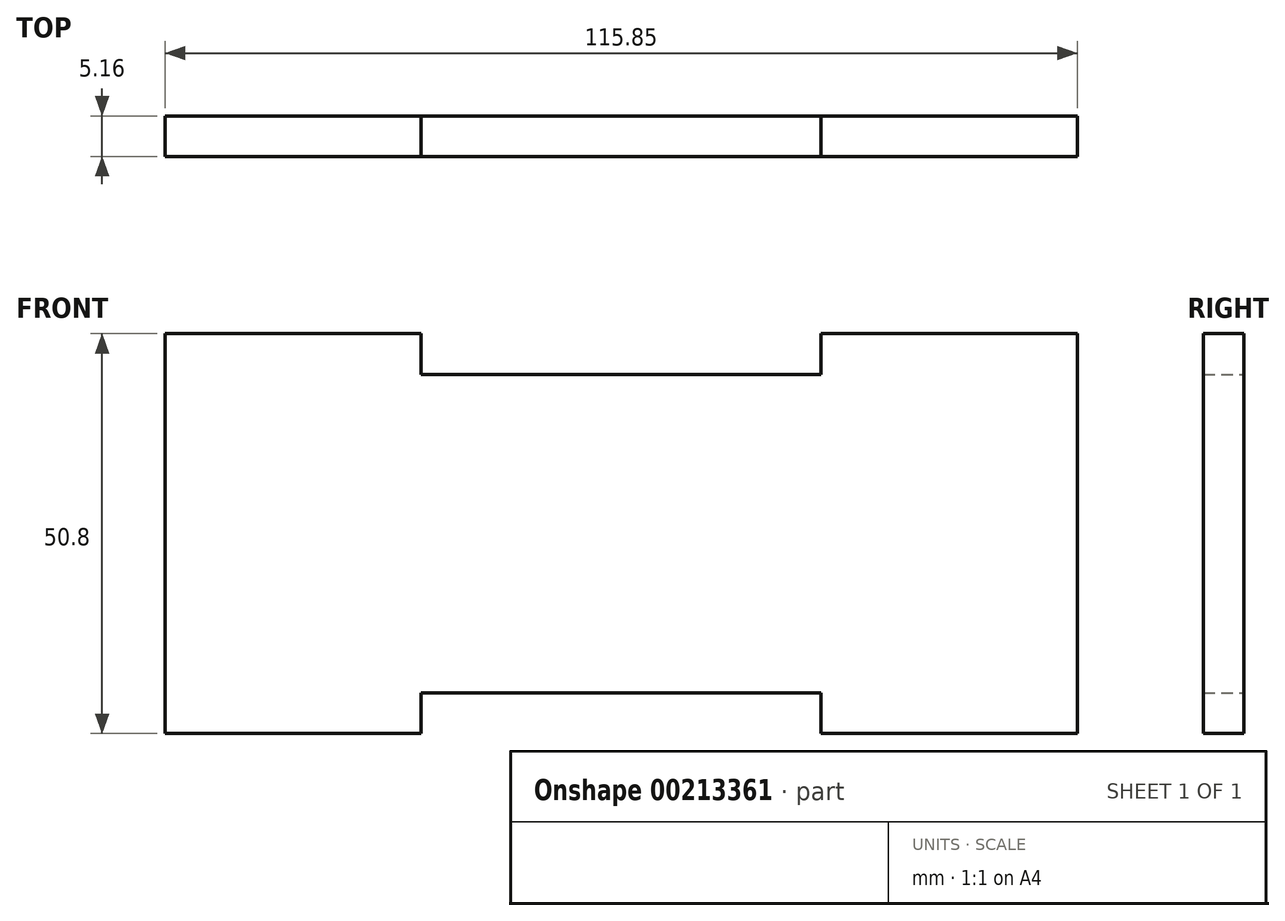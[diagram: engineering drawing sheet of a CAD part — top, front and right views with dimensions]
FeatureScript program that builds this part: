
annotation { "Feature Type Name" : "Feature", "Feature Type Description" : "" }
export const myFeature = defineFeature(function(context is Context, id is Id, definition is map)
    precondition{}
    {
        {
            var Q0;
            Q0=qCreatedBy(makeId("Front.planeOp"),FACE);
            var sketch = newSketch(context, id + "F0", { "sketchPlane" : qUnion([Q0])});
            skLineSegment(sketch, "E0.bottom", {"start": v(0, 0) * mm, "end": v(115.85, 0) * mm});
            skLineSegment(sketch, "E0.top", {"start": v(0, 50.8) * mm, "end": v(115.85, 50.8) * mm});
            skLineSegment(sketch, "E0.left", {"start": v(0, 0) * mm, "end": v(0, 50.8) * mm});
            skLineSegment(sketch, "E0.right", {"start": v(115.85, 0) * mm, "end": v(115.85, 50.8) * mm});
            skLineSegment(sketch, "E1.bottom", {"start": v(32.52, 50.8) * mm, "end": v(83.32, 50.8) * mm});
            skLineSegment(sketch, "E1.top", {"start": v(32.52, 45.64) * mm, "end": v(83.32, 45.64) * mm});
            skLineSegment(sketch, "E1.left", {"start": v(32.52, 50.8) * mm, "end": v(32.52, 45.64) * mm});
            skLineSegment(sketch, "E1.right", {"start": v(83.32, 50.8) * mm, "end": v(83.32, 45.64) * mm});
            skLineSegment(sketch, "E2.bottom", {"start": v(32.52, 0) * mm, "end": v(83.32, 0) * mm});
            skLineSegment(sketch, "E2.top", {"start": v(32.52, 5.16) * mm, "end": v(83.32, 5.16) * mm});
            skLineSegment(sketch, "E2.left", {"start": v(32.52, 0) * mm, "end": v(32.52, 5.16) * mm});
            skLineSegment(sketch, "E2.right", {"start": v(83.32, 0) * mm, "end": v(83.32, 5.16) * mm});
            skPoint(sketch, "E3", {"position": v(57.92, 45.64) * mm});
            skPoint(sketch, "E4", {"position": v(57.92, 5.16) * mm});
            skPoint(sketch, "E5", {"position": v(57.92, 50.8) * mm});
            skSolve(sketch);
        }
        {
            var Q0;
            {var subQ0=sQuery(id+"F0.wireOp",EDGE,"E0.left");Q0=makeQuery(id+"F0.imprint","IMPRINT",FACE,{"disambiguationData":[TD([[makeQuery(id+"F0.imprint","IMPRINT",EDGE,{"derivedFrom":subQ0}),-1.0]])]});}
            extrude(context, id + "F1", {"entities" : qUnion([Q0]), "depth" : 5.16 * mm});
        }
    });
